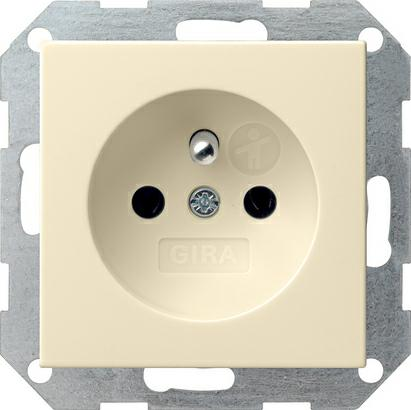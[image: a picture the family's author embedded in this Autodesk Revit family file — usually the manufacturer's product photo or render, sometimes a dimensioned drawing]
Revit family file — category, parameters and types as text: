
# Revit family: E_Cable Junction Box_F_MEPcontent_Spelsberg_IBTronic XL Drillbox 150_INT-EN
name_source: partatom
category: Electrical Fixtures
revit_build: Autodesk Revit 2017 (Build: 20160225_1515(x64)
units: mm (PartAtom-declared; Revit-internal decimal feet)

## family parameters
Cut with Voids When Loaded = No
Host = Face
Maintain Annotation Orientation = Yes
OmniClass Number = 23.80.30.14.24
OmniClass Title = Junction Boxes
Part Type = Junction Box
Room Calculation Point = No
Round Connector Dimension = Use Diameter
Shared = No

## types (2) — shared parameters
3D Representation = 3DGeometry
ETIM Article Class = EC000414
Height = 92 mm  [stored 0.301837 ft]
IFCExportAs = IfcJunctionBox
IFCExportType = NOTDEFINED
Length = 280 mm  [stored 0.918635 ft]
Manufacturer = Spelsberg
Manufacturer URL = http://www.spelsberg.com
Product Line = Spelsberg
Revit Version = 2017
Rotation U-Axis Correction = 0.00°
Rotation U-Axis Default Correction = 0.00°
Rotation V-Axis Correction = 0.00°
Rotation V-Axis Default Correction = 0.00°
Rotation W-Axis Correction = 0.00°
Rotation W-Axis Default Correction = 0.00°
Voltage = 230 V
Width = 252 mm  [stored 0.826772 ft]
zero-valued in all types: Default Elevation

## per-type parameters (varying)
| type | Article Description | Conduit Diameter 1 | Conduit Diameter 2 | Description | Manufacturer Art. No. | Side Distance | Side Offset |
| IBTronic XL Drillbox 150 | Enclosure IBTronic XL Drillbox | 20 mm  [stored 0.0656168 ft] | 25 mm  [stored 0.082021 ft] | Enclosure IBTronic XL Drillbox | 97680401 | 11 mm | 2 mm  [stored 0.00656168 ft] |
| IBTronic XL Drillbox 150 E | Enclosure IBTronic XL Drillbox E | 16 mm  [stored 0.0524934 ft] | 19 mm  [stored 0.062336 ft] | Enclosure IBTronic XL Drillbox E | 97680402 | 12 mm  [stored 0.0393701 ft] | 6 mm  [stored 0.019685 ft] |

note: column(s) folded — value = type name in every type: Article Type, Model

note: [stored X ft] marks values corroborated as IEEE doubles in the binary element streams (Revit-internal decimal feet)

## geometry (parser evidence)
native form markers: Sweep x17
no freeform markers — native parametric forms only
